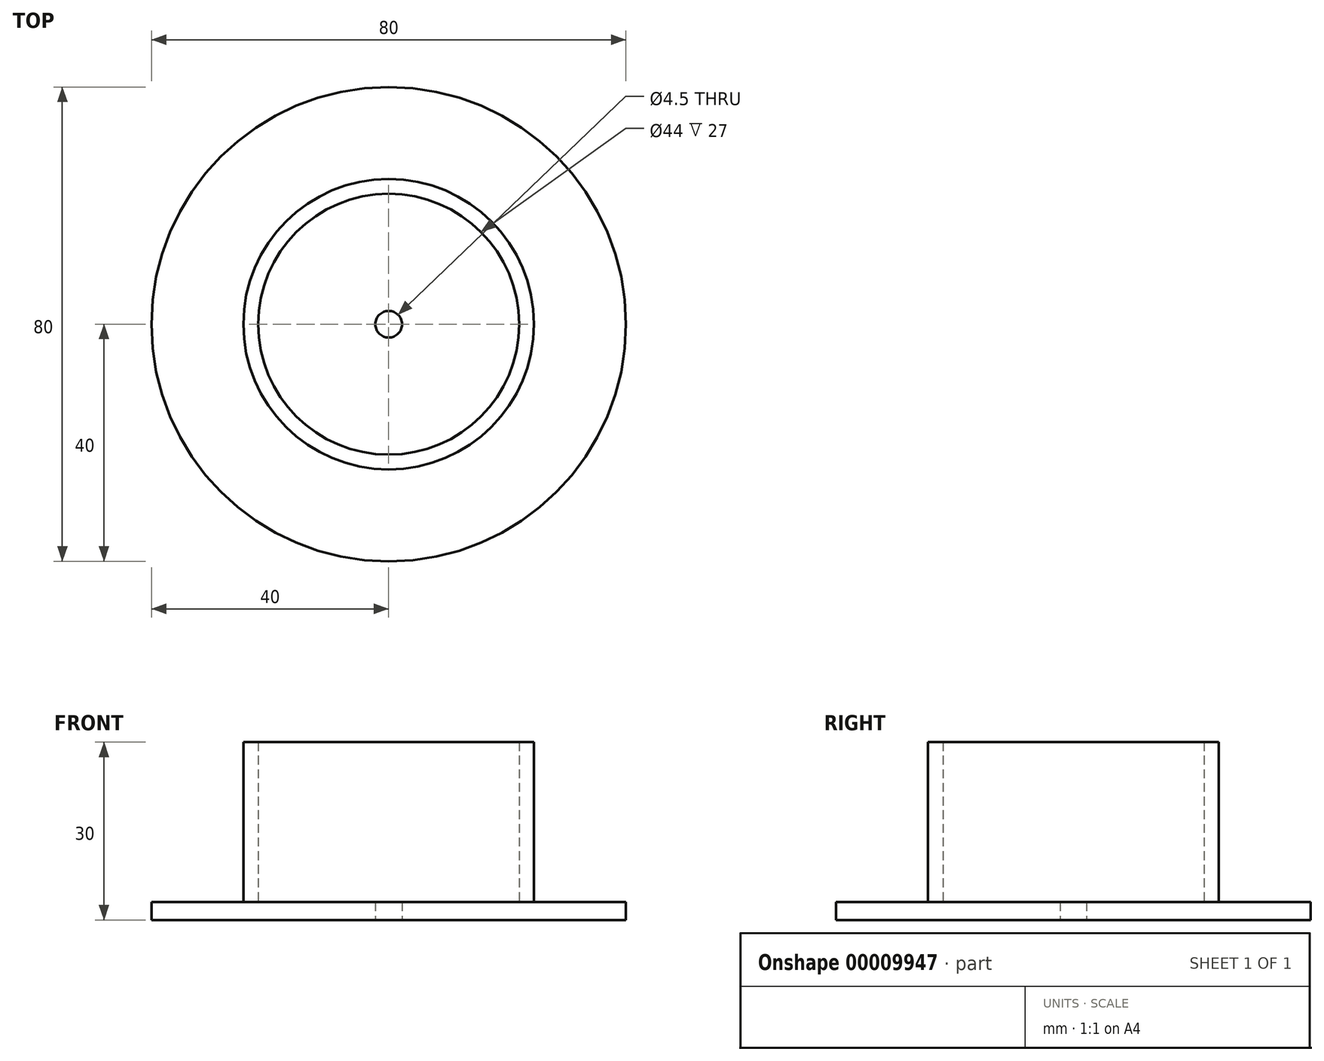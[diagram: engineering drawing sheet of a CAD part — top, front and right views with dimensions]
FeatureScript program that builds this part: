
annotation { "Feature Type Name" : "Feature", "Feature Type Description" : "" }
export const myFeature = defineFeature(function(context is Context, id is Id, definition is map)
    precondition{}
    {
        {
            var Q0;
            Q0=qCreatedBy(makeId("Top.planeOp"),FACE);
            var sketch = newSketch(context, id + "F0", { "sketchPlane" : qUnion([Q0])});
            skCircle(sketch, "E0", {"center": v(0, 0) * mm, "radius": 40 * mm});
            skCircle(sketch, "E1", {"center": v(0, 0) * mm, "radius": 22 * mm});
            skCircle(sketch, "E2", {"center": v(0, 0) * mm, "radius": 24.5 * mm});
            skCircle(sketch, "E3", {"center": v(0, 0) * mm, "radius": 2.25 * mm});
            skSolve(sketch);
        }
        {
            var Q0;
            Q0 = qSketchRegion(id + "F0", true);
            var Q1;
            Q1=makeQuery(id+"F0.imprint","IMPRINT",FACE,{"disambiguationData":[TD([[makeQuery(id+"F0.imprint","IMPRINT",EDGE,{"derivedFrom":sQuery(id+"F0.wireOp",EDGE,"E1")}),1.0]])]});
            var Q2;
            Q2=makeQuery(id+"F0.imprint","IMPRINT",FACE,{"disambiguationData":[TD([[makeQuery(id+"F0.imprint","IMPRINT",EDGE,{"derivedFrom":sQuery(id+"F0.wireOp",EDGE,"E1")}),-1.0]])]});
            extrude(context, id + "F1", {"entities" : qUnion([Q0, Q1, Q2]), "depth" : 3 * mm});
        }
        {
            var Q0;
            Q0=makeQuery(id+"F0.imprint","IMPRINT",FACE,{"disambiguationData":[TD([[makeQuery(id+"F0.imprint","IMPRINT",EDGE,{"derivedFrom":sQuery(id+"F0.wireOp",EDGE,"E1")}),-1.0]])]});
            extrude(context, id + "F2", {"entities" : qUnion([Q0]), "operationType" : NewBodyOperationType.ADD, "depth" : 30 * mm});
        }
        {
            var Q0;
            Q0=makeQuery(id+"F0.imprint","IMPRINT",FACE,{"disambiguationData":[TD([[makeQuery(id+"F0.imprint","IMPRINT",EDGE,{"derivedFrom":sQuery(id+"F0.wireOp",EDGE,"E0")}),1.0]])]});
            extrude(context, id + "F3", {"entities" : qUnion([Q0]), "operationType" : NewBodyOperationType.ADD, "depth" : 3 * mm});
        }
    });
